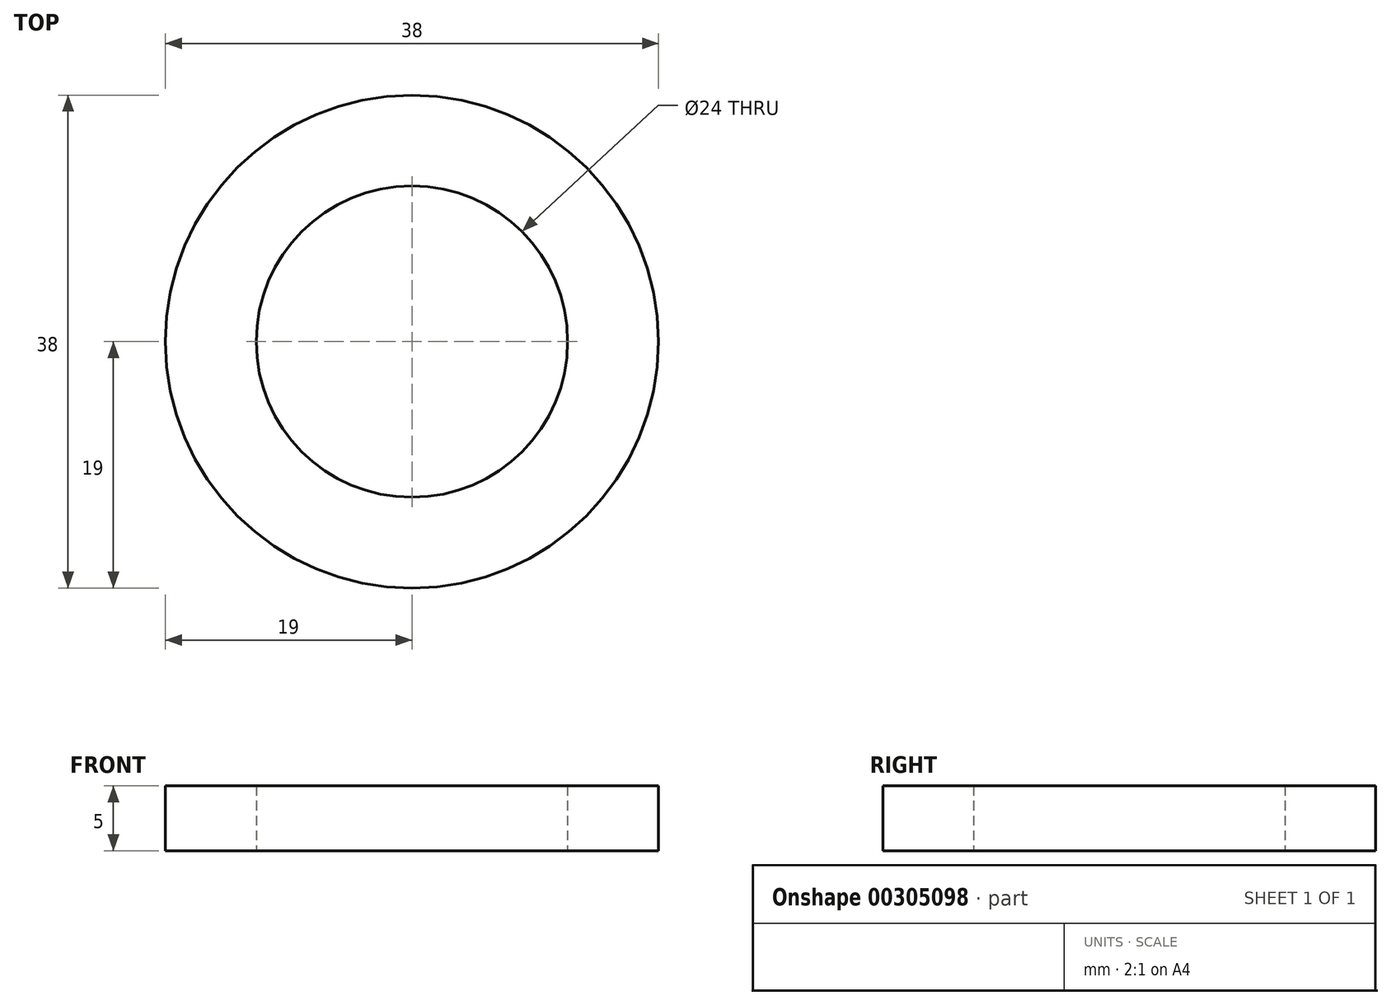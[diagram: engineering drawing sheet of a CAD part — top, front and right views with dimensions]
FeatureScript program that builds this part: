
annotation { "Feature Type Name" : "Feature", "Feature Type Description" : "" }
export const myFeature = defineFeature(function(context is Context, id is Id, definition is map)
    precondition{}
    {
        {
            var Q0;
            Q0=qCreatedBy(makeId("Top.planeOp"),FACE);
            var sketch = newSketch(context, id + "F0", { "sketchPlane" : qUnion([Q0])});
            skCircle(sketch, "E0", {"center": v(0, 0) * mm, "radius": 12 * mm});
            skCircle(sketch, "E1.0", {"center": v(0, 0) * mm, "radius": 19 * mm});
            skSolve(sketch);
        }
        {
            var Q0;
            Q0=makeQuery(id+"F0.imprint","IMPRINT",FACE,{"disambiguationData":[TD([[makeQuery(id+"F0.imprint","IMPRINT",EDGE,{"derivedFrom":sQuery(id+"F0.wireOp",EDGE,"E0")}),-1.0]])]});
            extrude(context, id + "F1", {"entities" : qUnion([Q0]), "depth" : 5 * mm});
        }
    });
